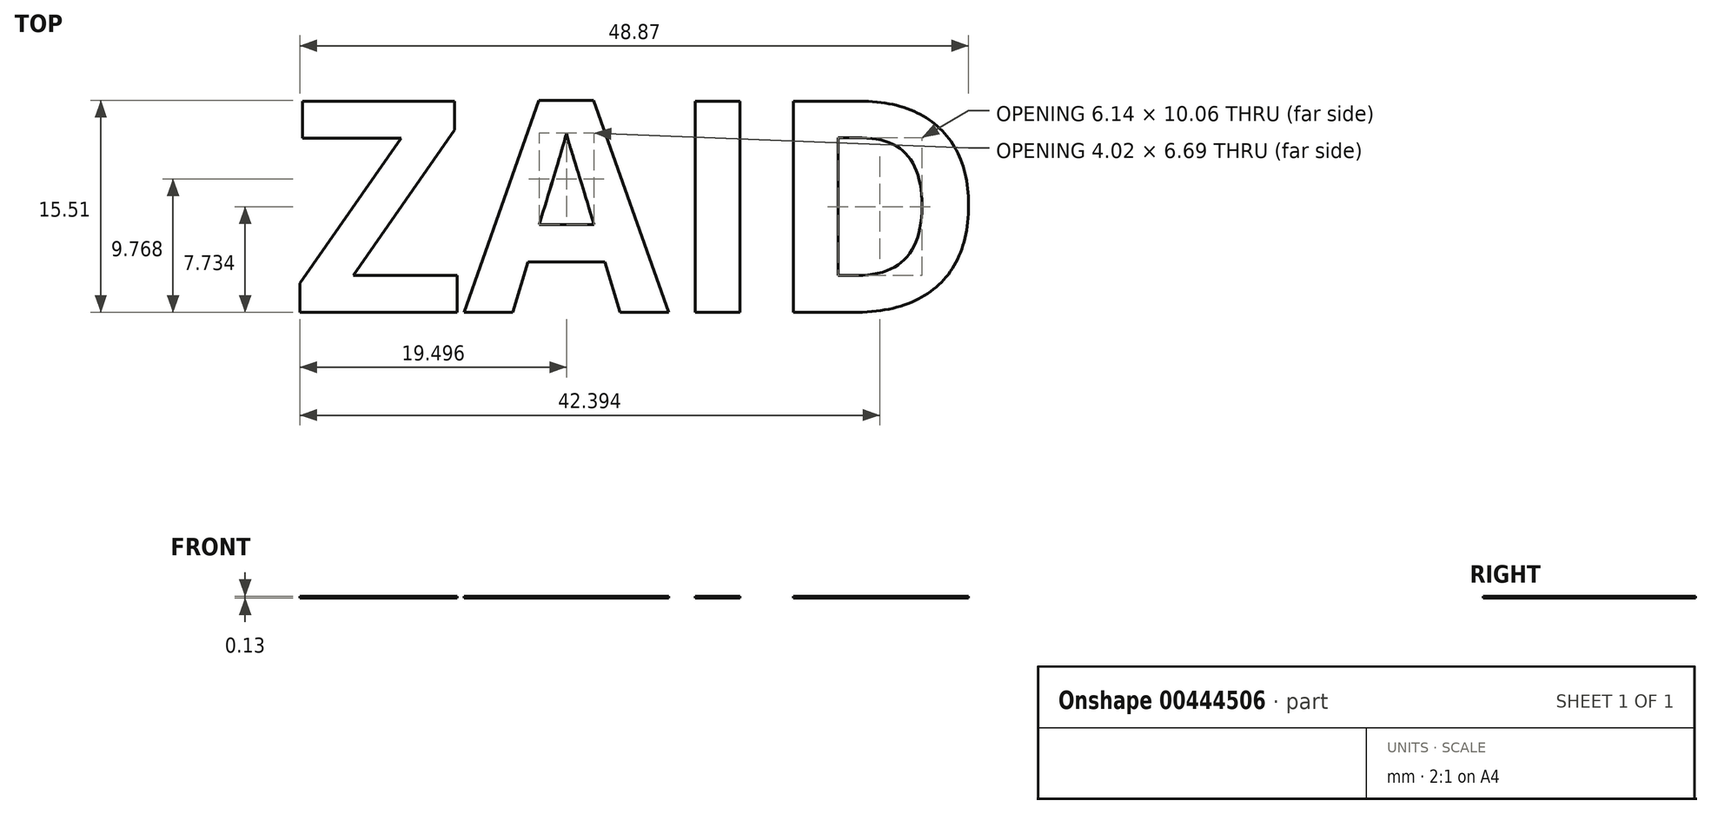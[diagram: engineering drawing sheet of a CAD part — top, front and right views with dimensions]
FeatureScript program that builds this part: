
annotation { "Feature Type Name" : "Feature", "Feature Type Description" : "" }
export const myFeature = defineFeature(function(context is Context, id is Id, definition is map)
    precondition{}
    {
        {
            var Q0;
            Q0=qCreatedBy(makeId("Top.planeOp"),FACE);
            var sketch = newSketch(context, id + "F0", { "sketchPlane" : qUnion([Q0])});
            skLineSegment(sketch, "E0.bottom", {"start": v(0, 0) * mm, "end": v(76.2, 0) * mm, "construction": true});
            skLineSegment(sketch, "E0.top", {"start": v(0, 76.2) * mm, "end": v(76.2, 76.2) * mm, "construction": true});
            skLineSegment(sketch, "E0.left", {"start": v(0, 0) * mm, "end": v(0, 76.2) * mm, "construction": true});
            skLineSegment(sketch, "E0.right", {"start": v(76.2, 0) * mm, "end": v(76.2, 76.2) * mm, "construction": true});
            skText(sketch, "E1", { "text": "ZAID", "fontName": "OpenSans-Bold.ttf"});
            const initialGuessF0  = {"E1": [0, 0, 1, 0, 0.01558]};
            skSetInitialGuess(sketch, initialGuessF0);
            skSolve(sketch);
        }
        {
            var Q0;
            Q0 = qSketchRegion(id + "F0", true);
            extrude(context, id + "F1", {"entities" : qUnion([Q0]), "depth" : 0.13 * mm});
        }
    });
